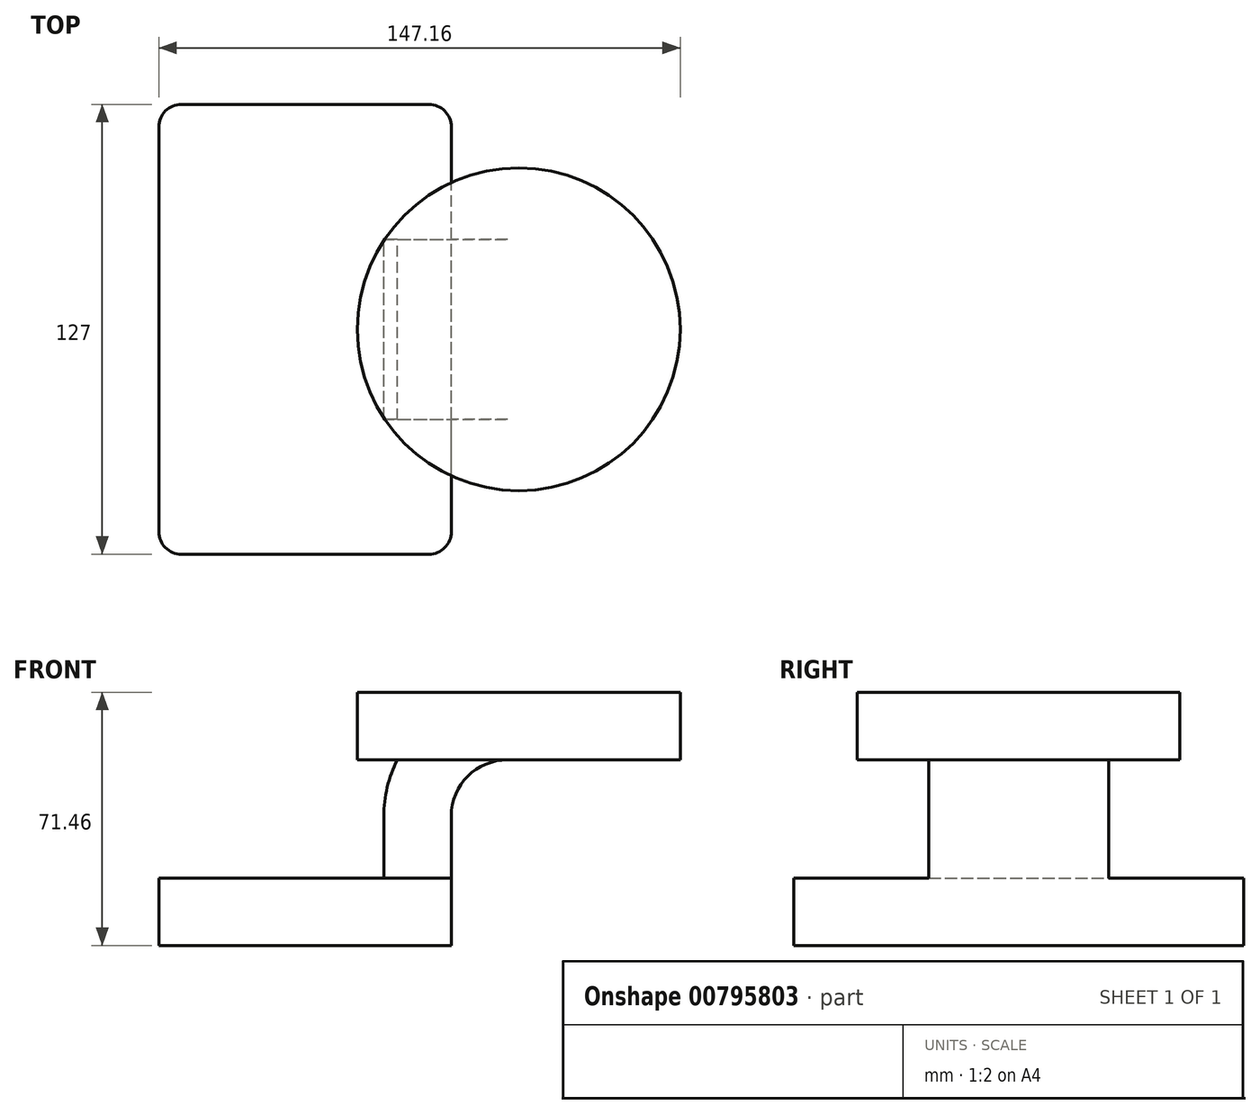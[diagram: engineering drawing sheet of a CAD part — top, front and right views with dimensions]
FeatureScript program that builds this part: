
annotation { "Feature Type Name" : "Feature", "Feature Type Description" : "" }
export const myFeature = defineFeature(function(context is Context, id is Id, definition is map)
    precondition{}
    {
        {
            var Q0;
            Q0=qCreatedBy(makeId("Front.planeOp"),FACE);
            var sketch = newSketch(context, id + "F0", { "sketchPlane" : qUnion([Q0])});
            skLineSegment(sketch, "E0.bottom", {"start": v(-41.28, 9.52) * mm, "end": v(41.28, 9.52) * mm});
            skLineSegment(sketch, "E0.top", {"start": v(-41.27, -9.53) * mm, "end": v(41.28, -9.53) * mm});
            skLineSegment(sketch, "E0.left", {"start": v(-41.28, 9.52) * mm, "end": v(-41.28, -9.53) * mm});
            skLineSegment(sketch, "E0.right", {"start": v(41.27, 9.53) * mm, "end": v(41.28, -9.52) * mm});
            skPoint(sketch, "E0.middle", {"position": v(0, 0) * mm});
            skLineSegment(sketch, "E1.bottom", {"start": v(60.32, 38.1) * mm, "end": v(111.12, 38.1) * mm});
            skLineSegment(sketch, "E1.top", {"start": v(60.32, 66.68) * mm, "end": v(111.12, 66.68) * mm});
            skLineSegment(sketch, "E1.left", {"start": v(60.32, 38.1) * mm, "end": v(60.32, 66.67) * mm});
            skLineSegment(sketch, "E1.right", {"start": v(111.13, 38.1) * mm, "end": v(111.12, 66.67) * mm});
            skPoint(sketch, "E1.middle", {"position": v(85.72, 52.39) * mm});
            skLineSegment(sketch, "E2", {"start": v(41.27, 9.53) * mm, "end": v(41.27, 27) * mm});
            skArc(sketch, "E3", {"start": v(41.27, 27) * mm, "mid": v(45.92, 38.23) * mm, "end": v(57.15, 42.88) * mm});
            skLineSegment(sketch, "E4", {"start": v(57.15, 42.88) * mm, "end": v(105.9, 42.88) * mm});
            skLineSegment(sketch, "E5.0", {"start": v(57.15, 61.93) * mm, "end": v(105.9, 61.93) * mm});
            skArc(sketch, "E5.1", {"start": v(22.22, 27) * mm, "mid": v(32.45, 51.7) * mm, "end": v(57.15, 61.93) * mm});
            skLineSegment(sketch, "E5.2", {"start": v(22.22, 9.53) * mm, "end": v(22.22, 27) * mm});
            skLineSegment(sketch, "E6", {"start": v(105.9, 38.1) * mm, "end": v(105.9, 66.68) * mm});
            skFitSpline(sketch, "E7", {"points": [v(-41.28, 9.53) * mm, v(57.15, 61.93) * mm], "startDerivative": vector(9.22, 102.68) * mm, "endDerivative": vector(104.1, -40.86) * mm});
            skSolve(sketch);
        }
        {
            var Q0;
            Q0=makeQuery(id+"F0.imprint","IMPRINT",FACE,{"disambiguationData":[TD([[makeQuery(id+"F0.imprint","IMPRINT",EDGE,{"derivedFrom":sQuery(id+"F0.wireOp",EDGE,"E0.top")}),1.0]])]});
            extrude(context, id + "F1", {"entities" : qUnion([Q0]), "endBound" : BoundingType.SYMMETRIC, "depth" : 127 * mm, "offsetDistance" : 25.4 * mm});
        }
        {
            var Q0;
            {var subQ1=sQuery(id+"F0.wireOp",EDGE,"E2");Q0=makeQuery(id+"F0.imprint","IMPRINT",FACE,{"disambiguationData":[TD([[makeQuery(id+"F0.imprint","IMPRINT",EDGE,{"derivedFrom":subQ1}),1.0]])]});}
            extrude(context, id + "F2", {"entities" : qUnion([Q0]), "operationType" : NewBodyOperationType.ADD, "endBound" : BoundingType.SYMMETRIC, "depth" : 50.8 * mm, "offsetDistance" : 25.4 * mm});
        }
        {
            var Q0;
            Q0=makeQuery(id+"F0.imprint","IMPRINT",FACE,{"disambiguationData":[TD([[makeQuery(id+"F0.imprint","IMPRINT",EDGE,{"derivedFrom":sQuery(id+"F0.wireOp",EDGE,"E5.1")}),1.0]])]});
            extrude(context, id + "F3", {"entities" : qUnion([Q0]), "operationType" : NewBodyOperationType.ADD, "endBound" : BoundingType.SYMMETRIC, "depth" : 15.88 * mm, "offsetDistance" : 25.4 * mm});
        }
        {
            var Q0;
            {var subQ0=sQuery(id+"F0.wireOp",EDGE,"E4");var subQ1=sQuery(id+"F0.wireOp",EDGE,"E1.left");var subQ2=makeQuery(id+"F0.imprint","INTERSECT",VERTEX,{"derivedFrom":[subQ1,subQ0]});Q0=makeQuery(id+"F0.imprint","IMPRINT",FACE,{"disambiguationData":[TD([[makeQuery(id+"F0.imprint","IMPRINT",EDGE,{"disambiguationData":[TD([[subQ2,-1.0]])],"derivedFrom":subQ1}),-1.0]])]});}
            var Q1;
            Q1=sQuery(id+"F0.wireOp",EDGE,"E1.left");
            revolve(context, id + "F4", {"operationType" : NewBodyOperationType.ADD, "surfaceOperationType" : NewSurfaceOperationType.NEW, "entities" : qUnion([Q0]), "axis" : qUnion([Q1]), "revolveType" : RevolveType.FULL});
        }
        {
            var Q0;
            Q0=makeQuery(id+"F1.opExtrude","CAP_EDGE",EDGE,{"disambiguationData":[OSD([sQuery(id+"F0.wireOp",EDGE,"E0.right")])],"isStart":false});
            var Q1;
            Q1=makeQuery(id+"F1.opExtrude","CAP_EDGE",EDGE,{"disambiguationData":[OSD([sQuery(id+"F0.wireOp",EDGE,"E0.left")])],"isStart":false});
            var Q2;
            Q2=makeQuery(id+"F1.opExtrude","CAP_EDGE",EDGE,{"disambiguationData":[OSD([sQuery(id+"F0.wireOp",EDGE,"E0.right")])],"isStart":true});
            var Q3;
            Q3=makeQuery(id+"F1.opExtrude","CAP_EDGE",EDGE,{"disambiguationData":[OSD([sQuery(id+"F0.wireOp",EDGE,"E0.left")])],"isStart":true});
            fillet(context, id + "F5", {"entities" : qUnion([Q0, Q1, Q2, Q3]), "radius" : 6.35 * mm, "tangentPropagation" : true, "allowEdgeOverflow" : false});
        }
    });
